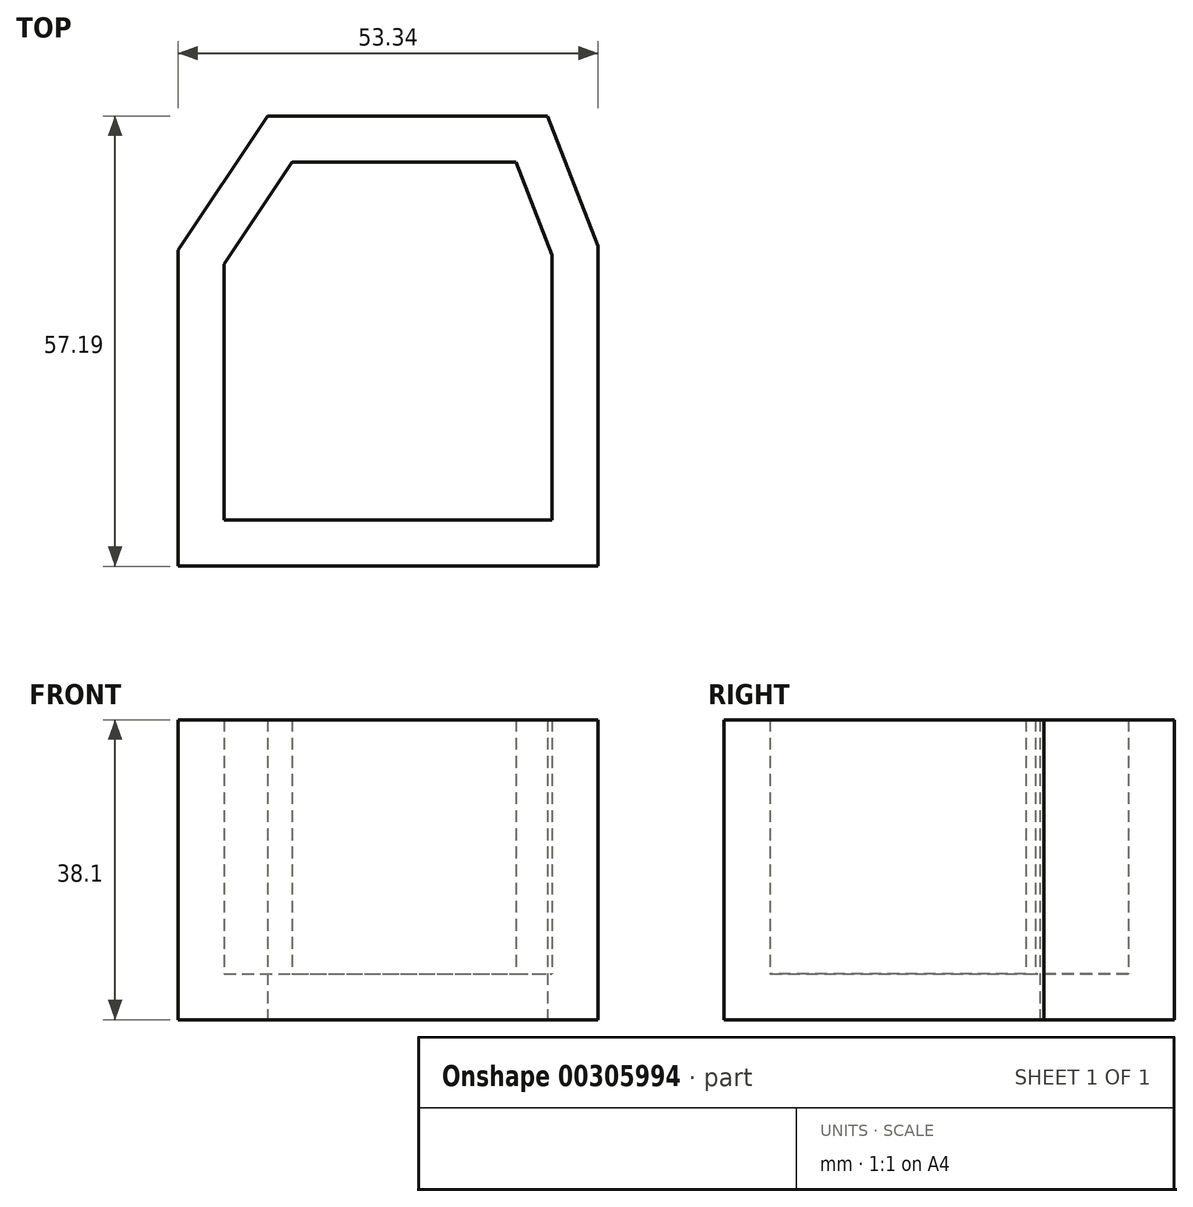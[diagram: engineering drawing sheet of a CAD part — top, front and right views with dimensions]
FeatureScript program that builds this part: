
annotation { "Feature Type Name" : "Feature", "Feature Type Description" : "" }
export const myFeature = defineFeature(function(context is Context, id is Id, definition is map)
    precondition{}
    {
        {
            var Q0;
            Q0=qCreatedBy(makeId("Top.planeOp"),FACE);
            var sketch = newSketch(context, id + "F0", { "sketchPlane" : qUnion([Q0])});
            skLineSegment(sketch, "E0", {"start": v(-44.97, 6.7) * mm, "end": v(-44.97, -33.45) * mm});
            skLineSegment(sketch, "E1", {"start": v(-44.97, -33.45) * mm, "end": v(8.37, -33.45) * mm});
            skLineSegment(sketch, "E2", {"start": v(8.37, -33.45) * mm, "end": v(8.37, 7.2) * mm});
            skLineSegment(sketch, "E3", {"start": v(-44.97, 6.7) * mm, "end": v(-33.6, 23.74) * mm});
            skLineSegment(sketch, "E4", {"start": v(-33.6, 23.74) * mm, "end": v(1.95, 23.74) * mm});
            skLineSegment(sketch, "E5", {"start": v(1.95, 23.74) * mm, "end": v(8.37, 7.2) * mm});
            skLineSegment(sketch, "E6.0", {"start": v(-38.62, 4.78) * mm, "end": v(-38.62, -27.1) * mm});
            skLineSegment(sketch, "E6.1", {"start": v(2.02, -27.1) * mm, "end": v(2.02, 6) * mm});
            skLineSegment(sketch, "E6.2", {"start": v(-2.4, 17.39) * mm, "end": v(2.02, 6) * mm});
            skLineSegment(sketch, "E6.3", {"start": v(-38.62, -27.1) * mm, "end": v(2.02, -27.1) * mm});
            skLineSegment(sketch, "E6.4", {"start": v(-30.2, 17.39) * mm, "end": v(-2.4, 17.39) * mm});
            skLineSegment(sketch, "E6.5", {"start": v(-38.62, 4.78) * mm, "end": v(-30.2, 17.39) * mm});
            skSolve(sketch);
        }
        {
            var Q0;
            Q0=makeQuery(id+"F0.imprint","IMPRINT",FACE,{"disambiguationData":[TD([[makeQuery(id+"F0.imprint","IMPRINT",EDGE,{"derivedFrom":sQuery(id+"F0.wireOp",EDGE,"E6.0")}),1.0]])]});
            var Q1;
            Q1=makeQuery(id+"F0.imprint","IMPRINT",FACE,{"disambiguationData":[TD([[makeQuery(id+"F0.imprint","IMPRINT",EDGE,{"derivedFrom":sQuery(id+"F0.wireOp",EDGE,"E0")}),1.0]])]});
            extrude(context, id + "F1", {"entities" : qUnion([Q0, Q1]), "depth" : 38.1 * mm});
        }
        {
            var Q0;
            Q0=makeQuery(id+"F1.opExtrude","CAP_FACE",FACE,{"disambiguationData":[OSD([sQuery(id+"F0.wireOp",EDGE,"E0"),sQuery(id+"F0.wireOp",EDGE,"E1"),sQuery(id+"F0.wireOp",EDGE,"E2"),sQuery(id+"F0.wireOp",EDGE,"E3"),sQuery(id+"F0.wireOp",EDGE,"E4"),sQuery(id+"F0.wireOp",EDGE,"E5")])],"isStart":false});
            shell(context, id + "F2", {"entities" : qUnion([Q0]), "thickness" : 5.84 * mm});
        }
    });
